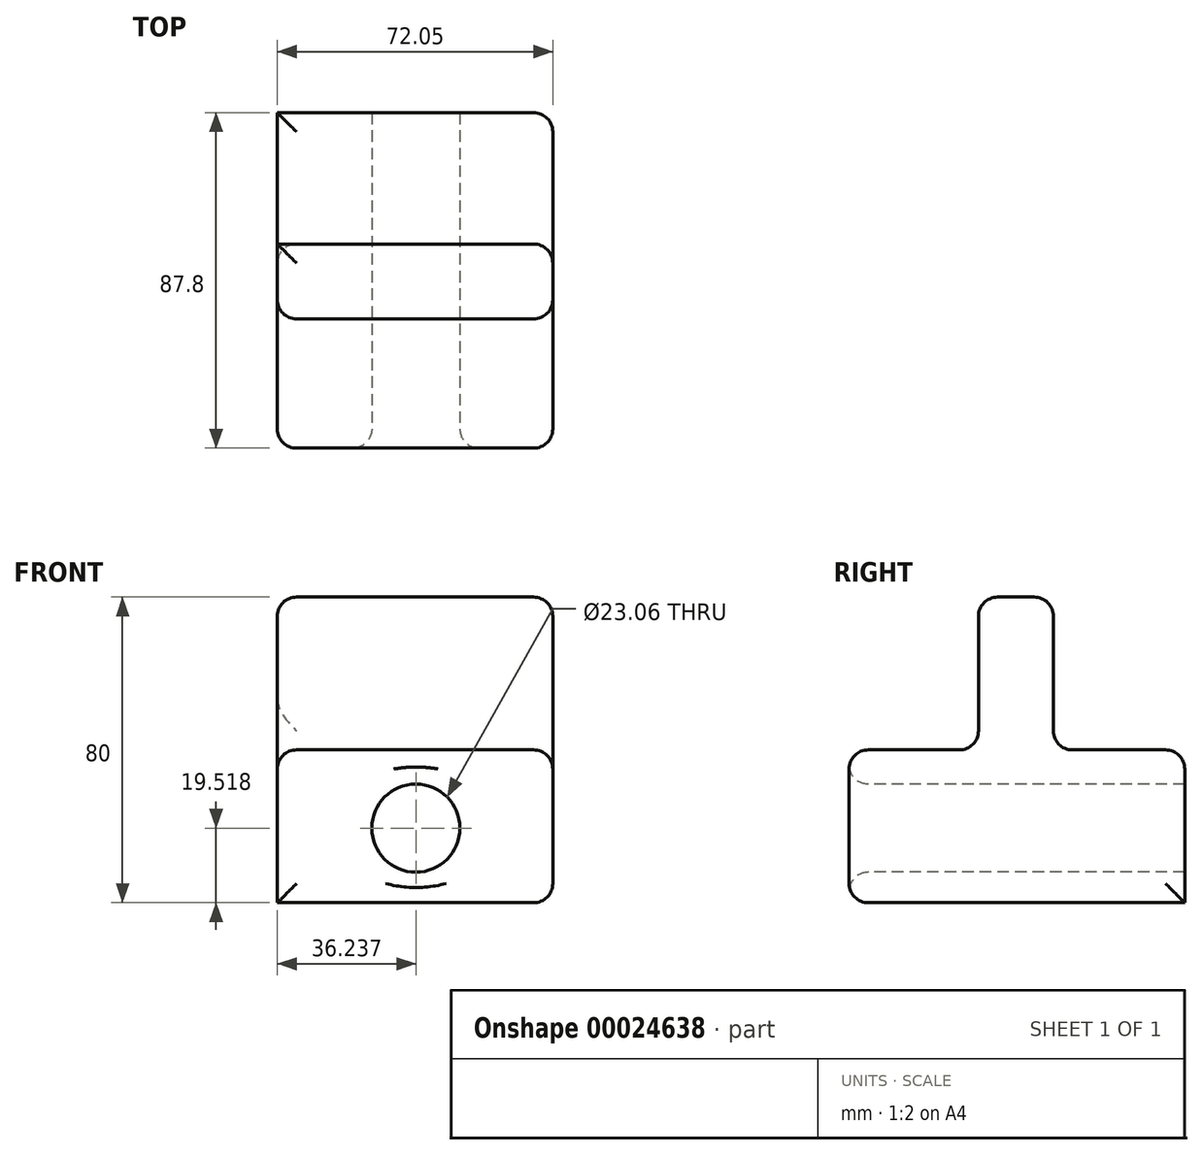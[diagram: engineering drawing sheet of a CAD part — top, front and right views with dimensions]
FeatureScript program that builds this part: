
annotation { "Feature Type Name" : "Feature", "Feature Type Description" : "" }
export const myFeature = defineFeature(function(context is Context, id is Id, definition is map)
    precondition{}
    {
        {
            var Q0;
            Q0=qCreatedBy(makeId("Top.planeOp"),FACE);
            var sketch = newSketch(context, id + "F0", { "sketchPlane" : qUnion([Q0])});
            skLineSegment(sketch, "E0.bottom", {"start": v(-59.89, -44.54) * mm, "end": v(12.16, -44.54) * mm});
            skLineSegment(sketch, "E0.top", {"start": v(-59.89, 43.26) * mm, "end": v(12.16, 43.26) * mm});
            skLineSegment(sketch, "E0.left", {"start": v(-59.89, -44.54) * mm, "end": v(-59.89, 43.26) * mm});
            skLineSegment(sketch, "E0.right", {"start": v(12.16, -44.54) * mm, "end": v(12.16, 43.26) * mm});
            skSolve(sketch);
        }
        {
            var Q0;
            Q0=makeQuery(id+"F0.imprint","IMPRINT",FACE,{"disambiguationData":[TD([[makeQuery(id+"F0.imprint","IMPRINT",EDGE,{"derivedFrom":sQuery(id+"F0.wireOp",EDGE,"E0.bottom")}),1.0]])]});
            extrude(context, id + "F1", {"entities" : qUnion([Q0]), "depth" : 40 * mm});
        }
        {
            var Q0;
            Q0=makeQuery(id+"F1.opExtrude","SWEPT_FACE",FACE,{"disambiguationData":[OSD([sQuery(id+"F0.wireOp",EDGE,"E0.bottom")])]});
            var sketch = newSketch(context, id + "F2", { "sketchPlane" : qUnion([Q0])});
            skCircle(sketch, "E1", {"center": v(-23.65, 19.52) * mm, "radius": 11.53 * mm});
            skSolve(sketch);
        }
        {
            var Q0;
            Q0=makeQuery(id+"F2.imprint","IMPRINT",FACE,{"disambiguationData":[TD([[makeQuery(id+"F2.imprint","IMPRINT",EDGE,{"derivedFrom":sQuery(id+"F2.wireOp",EDGE,"E1")}),1.0]])]});
            extrude(context, id + "F3", {"entities" : qUnion([Q0]), "operationType" : NewBodyOperationType.REMOVE, "endBound" : BoundingType.THROUGH_ALL, "oppositeDirection" : true, "depth" : 25 * mm});
        }
        {
            var Q0;
            Q0=makeQuery(id+"F1.opExtrude","CAP_FACE",FACE,{"disambiguationData":[OSD([sQuery(id+"F0.wireOp",EDGE,"E0.bottom"),sQuery(id+"F0.wireOp",EDGE,"E0.top"),sQuery(id+"F0.wireOp",EDGE,"E0.left"),sQuery(id+"F0.wireOp",EDGE,"E0.right")])],"isStart":false});
            var sketch = newSketch(context, id + "F4", { "sketchPlane" : qUnion([Q0])});
            skLineSegment(sketch, "E2.bottom", {"start": v(-59.89, -10.7) * mm, "end": v(12.16, -10.7) * mm});
            skLineSegment(sketch, "E2.top", {"start": v(-59.89, 8.88) * mm, "end": v(12.16, 8.88) * mm});
            skLineSegment(sketch, "E2.left", {"start": v(-59.89, -10.7) * mm, "end": v(-59.89, 8.88) * mm});
            skLineSegment(sketch, "E2.right", {"start": v(12.16, -10.7) * mm, "end": v(12.16, 8.88) * mm});
            skSolve(sketch);
        }
        {
            var Q0;
            Q0=makeQuery(id+"F4.imprint","IMPRINT",FACE,{"disambiguationData":[TD([[makeQuery(id+"F4.imprint","IMPRINT",EDGE,{"derivedFrom":sQuery(id+"F4.wireOp",EDGE,"E2.bottom")}),1.0]])]});
            extrude(context, id + "F5", {"entities" : qUnion([Q0]), "operationType" : NewBodyOperationType.ADD, "depth" : 40 * mm});
        }
        {
            var Q0;
            Q0=makeQuery(id+"F5.opExtrude","SWEPT_FACE",FACE,{"disambiguationData":[OSD([sQuery(id+"F4.wireOp",EDGE,"E2.bottom")])]});
            var Q1;
            {var subQ0=sQuery(id+"F0.wireOp",EDGE,"E0.bottom");var subQ1=sQuery(id+"F0.wireOp",EDGE,"E0.left");var subQ2=sQuery(id+"F0.wireOp",EDGE,"E0.right");Q1=makeQuery(id+"F5.boolean.opBoolean","SPLIT",FACE,{"disambiguationData":[TD([makeQuery(id+"F1.opExtrude","SWEPT_FACE",FACE,{"disambiguationData":[OSD([subQ0])]})])],"derivedFrom":makeQuery(id+"F1.opExtrude","CAP_FACE",FACE,{"disambiguationData":[OSD([subQ0,sQuery(id+"F0.wireOp",EDGE,"E0.top"),subQ1,subQ2])],"isStart":false})});}
            var Q2;
            Q2=makeQuery(id+"F1.opExtrude","SWEPT_FACE",FACE,{"disambiguationData":[OSD([sQuery(id+"F0.wireOp",EDGE,"E0.bottom")])]});
            var Q3;
            Q3=makeQuery(id+"F5.boolean.opBoolean","MERGE",FACE,{"derivedFrom":[makeQuery(id+"F1.opExtrude","SWEPT_FACE",FACE,{"disambiguationData":[OSD([sQuery(id+"F0.wireOp",EDGE,"E0.right")])]}),makeQuery(id+"F5.opExtrude","SWEPT_FACE",FACE,{"disambiguationData":[OSD([sQuery(id+"F4.wireOp",EDGE,"E2.right")])]})]});
            var Q4;
            Q4=makeQuery(id+"F5.opExtrude","CAP_FACE",FACE,{"disambiguationData":[OSD([sQuery(id+"F4.wireOp",EDGE,"E2.bottom"),sQuery(id+"F4.wireOp",EDGE,"E2.top"),sQuery(id+"F4.wireOp",EDGE,"E2.left"),sQuery(id+"F4.wireOp",EDGE,"E2.right")])],"isStart":false});
            var Q5;
            {var subQ0=sQuery(id+"F0.wireOp",EDGE,"E0.top");var subQ1=sQuery(id+"F0.wireOp",EDGE,"E0.left");var subQ2=sQuery(id+"F0.wireOp",EDGE,"E0.right");Q5=makeQuery(id+"F5.boolean.opBoolean","SPLIT",FACE,{"disambiguationData":[TD([makeQuery(id+"F1.opExtrude","SWEPT_FACE",FACE,{"disambiguationData":[OSD([subQ0])]})])],"derivedFrom":makeQuery(id+"F1.opExtrude","CAP_FACE",FACE,{"disambiguationData":[OSD([sQuery(id+"F0.wireOp",EDGE,"E0.bottom"),subQ0,subQ1,subQ2])],"isStart":false})});}
            fillet(context, id + "F6", {"entities" : qUnion([Q0, Q1, Q2, Q3, Q4, Q5]), "radius" : 5 * mm, "tangentPropagation" : true, "allowEdgeOverflow" : false});
        }
    });
